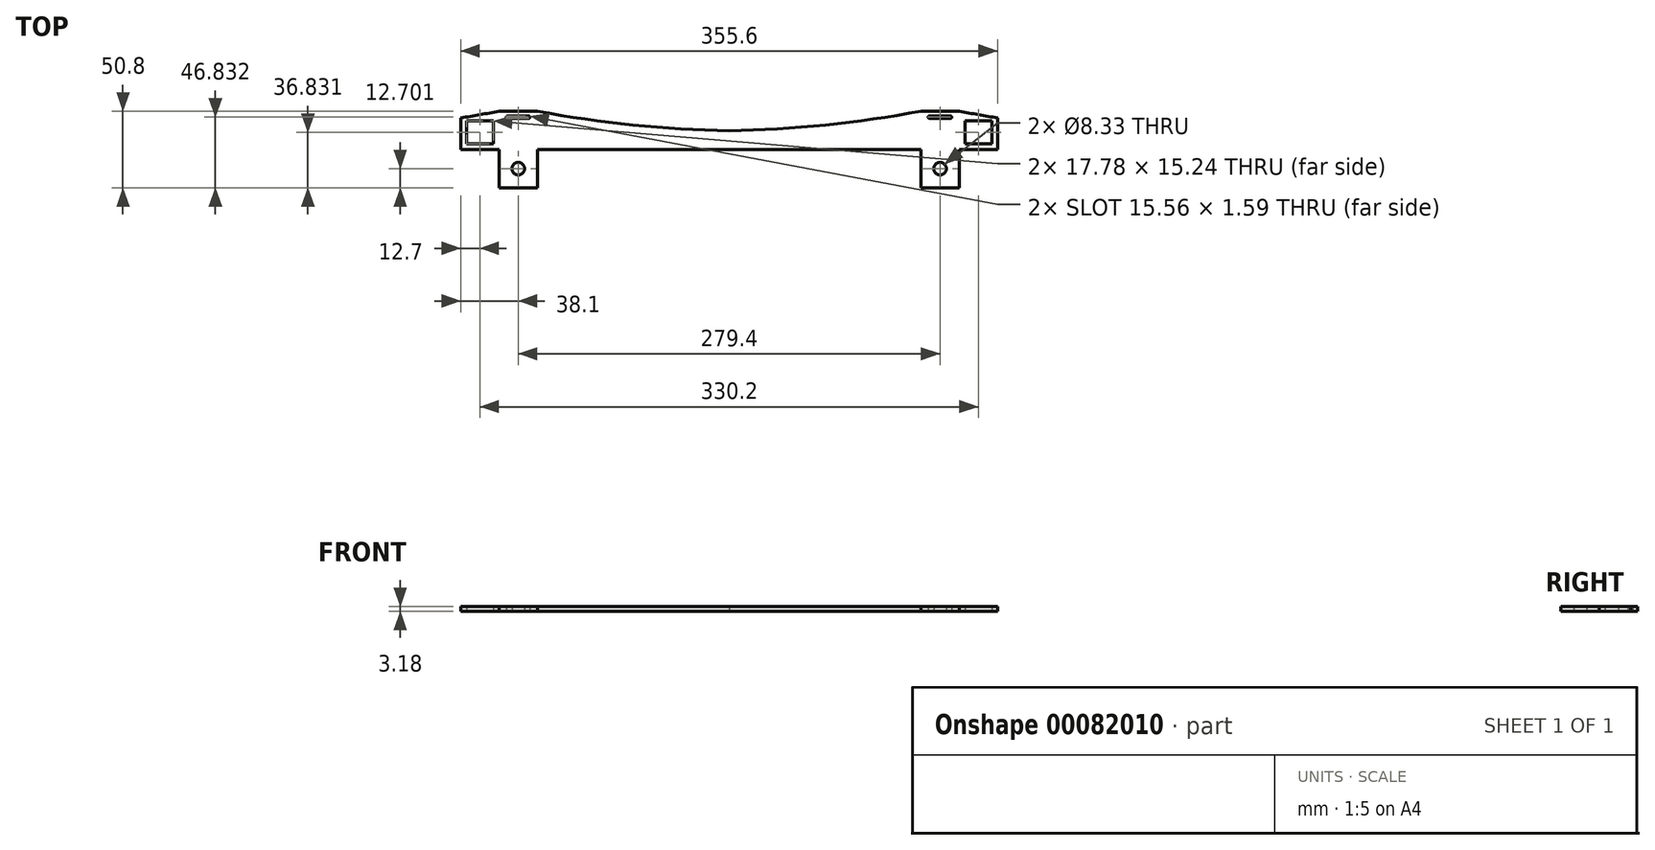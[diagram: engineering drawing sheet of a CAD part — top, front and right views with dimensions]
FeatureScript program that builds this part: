
annotation { "Feature Type Name" : "Feature", "Feature Type Description" : "" }
export const myFeature = defineFeature(function(context is Context, id is Id, definition is map)
    precondition{}
    {
        {
            var Q0;
            Q0=qCreatedBy(makeId("Top.planeOp"),FACE);
            var sketch = newSketch(context, id + "F0", { "sketchPlane" : qUnion([Q0])});
            skLineSegment(sketch, "E0", {"start": v(25.4, 0.27) * mm, "end": v(25.4, 25.67) * mm});
            skLineSegment(sketch, "E1", {"start": v(50.8, 25.67) * mm, "end": v(177.8, 25.67) * mm});
            skLineSegment(sketch, "E2", {"start": v(25.4, 51.07) * mm, "end": v(50.8, 51.07) * mm});
            skArc(sketch, "E3", {"start": v(50.8, 51.07) * mm, "mid": v(114.03, 41.92) * mm, "end": v(177.8, 38.1) * mm});
            skLineSegment(sketch, "E4", {"start": v(177.8, 92.1) * mm, "end": v(177.8, -8.52) * mm, "construction": true});
            skLineSegment(sketch, "E5", {"start": v(25.4, 51.07) * mm, "end": v(25.4, 25.67) * mm, "construction": true});
            skLineSegment(sketch, "E6", {"start": v(50.8, 51.07) * mm, "end": v(50.8, 25.67) * mm, "construction": true});
            skArc(sketch, "E7", {"start": v(31.12, 47.9) * mm, "mid": v(30.32, 47.1) * mm, "end": v(31.12, 46.3) * mm});
            skArc(sketch, "E8.MirrorC", {"start": v(45.09, 47.9) * mm, "mid": v(45.88, 47.1) * mm, "end": v(45.09, 46.3) * mm});
            skLineSegment(sketch, "E9", {"start": v(31.12, 47.9) * mm, "end": v(45.09, 47.9) * mm});
            skLineSegment(sketch, "E10", {"start": v(45.09, 46.3) * mm, "end": v(31.12, 46.3) * mm});
            skLineSegment(sketch, "E11", {"start": v(0, 25.67) * mm, "end": v(0, 46.6) * mm});
            skLineSegment(sketch, "E12.bottom", {"start": v(21.59, 44.72) * mm, "end": v(3.8, 44.72) * mm});
            skLineSegment(sketch, "E12.top", {"start": v(21.59, 29.48) * mm, "end": v(3.8, 29.48) * mm});
            skLineSegment(sketch, "E12.right", {"start": v(3.8, 44.72) * mm, "end": v(3.8, 29.48) * mm});
            skArc(sketch, "E13", {"start": v(0, 46.6) * mm, "mid": v(12.72, 48.73) * mm, "end": v(25.4, 51.07) * mm});
            skLineSegment(sketch, "E14.MirrorCS", {"start": v(50.8, 25.67) * mm, "end": v(50.8, 0.27) * mm});
            skCircle(sketch, "E15.MirrorC", {"center": v(38.1, 12.97) * mm, "radius": 4.17 * mm});
            skLineSegment(sketch, "E16.MirrorCS", {"start": v(50.8, 0.27) * mm, "end": v(25.4, 0.27) * mm});
            skLineSegment(sketch, "E17", {"start": v(50.8, 25.67) * mm, "end": v(25.4, 25.67) * mm, "construction": true});
            skLineSegment(sketch, "E18", {"start": v(0, 25.67) * mm, "end": v(25.4, 25.67) * mm});
            skLineSegment(sketch, "E19", {"start": v(21.59, 44.72) * mm, "end": v(21.59, 29.48) * mm});
            skArc(sketch, "E20.MirrorCS", {"start": v(324.48, 47.9) * mm, "mid": v(325.28, 47.1) * mm, "end": v(324.48, 46.3) * mm});
            skArc(sketch, "E21.MirrorCS", {"start": v(310.51, 47.9) * mm, "mid": v(309.72, 47.1) * mm, "end": v(310.51, 46.3) * mm});
            skLineSegment(sketch, "E22.MirrorCS", {"start": v(330.2, 0.27) * mm, "end": v(330.2, 25.67) * mm});
            skLineSegment(sketch, "E23.MirrorCS", {"start": v(304.8, 25.67) * mm, "end": v(177.8, 25.67) * mm});
            skLineSegment(sketch, "E24.MirrorCS", {"start": v(351.79, 44.72) * mm, "end": v(351.79, 29.48) * mm});
            skLineSegment(sketch, "E25.MirrorCS", {"start": v(334.01, 44.72) * mm, "end": v(334.01, 29.48) * mm});
            skLineSegment(sketch, "E26.MirrorCS", {"start": v(304.8, 25.67) * mm, "end": v(304.8, 0.27) * mm});
            skLineSegment(sketch, "E27.MirrorCS", {"start": v(304.8, 0.27) * mm, "end": v(330.2, 0.27) * mm});
            skLineSegment(sketch, "E28.MirrorCS", {"start": v(355.6, 25.67) * mm, "end": v(330.2, 25.67) * mm});
            skLineSegment(sketch, "E29.MirrorCS", {"start": v(334.01, 44.72) * mm, "end": v(351.8, 44.72) * mm});
            skLineSegment(sketch, "E30.MirrorCS", {"start": v(355.6, 25.67) * mm, "end": v(355.6, 46.6) * mm});
            skLineSegment(sketch, "E31.MirrorCS", {"start": v(310.51, 46.3) * mm, "end": v(324.48, 46.3) * mm});
            skLineSegment(sketch, "E32.MirrorCS", {"start": v(324.48, 47.9) * mm, "end": v(310.51, 47.9) * mm});
            skLineSegment(sketch, "E33.MirrorCS", {"start": v(304.8, 51.07) * mm, "end": v(304.8, 25.67) * mm, "construction": true});
            skArc(sketch, "E34.MirrorCS", {"start": v(304.8, 51.07) * mm, "mid": v(241.57, 41.92) * mm, "end": v(177.8, 38.1) * mm});
            skLineSegment(sketch, "E35.MirrorCS", {"start": v(330.2, 51.07) * mm, "end": v(304.8, 51.07) * mm});
            skLineSegment(sketch, "E36.MirrorCS", {"start": v(304.8, 25.67) * mm, "end": v(330.2, 25.67) * mm, "construction": true});
            skLineSegment(sketch, "E37.MirrorCS", {"start": v(330.2, 51.07) * mm, "end": v(330.2, 25.67) * mm, "construction": true});
            skCircle(sketch, "E38.MirrorC", {"center": v(317.5, 12.97) * mm, "radius": 4.17 * mm});
            skArc(sketch, "E39.MirrorCS", {"start": v(355.6, 46.6) * mm, "mid": v(342.88, 48.73) * mm, "end": v(330.2, 51.07) * mm});
            skLineSegment(sketch, "E40.MirrorCS", {"start": v(334.01, 29.48) * mm, "end": v(351.8, 29.48) * mm});
            skSolve(sketch);
        }
        {
            var Q0;
            Q0 = qSketchRegion(id + "F0", true);
            extrude(context, id + "F1", {"entities" : qUnion([Q0]), "depth" : 3.17 * mm});
        }
    });
